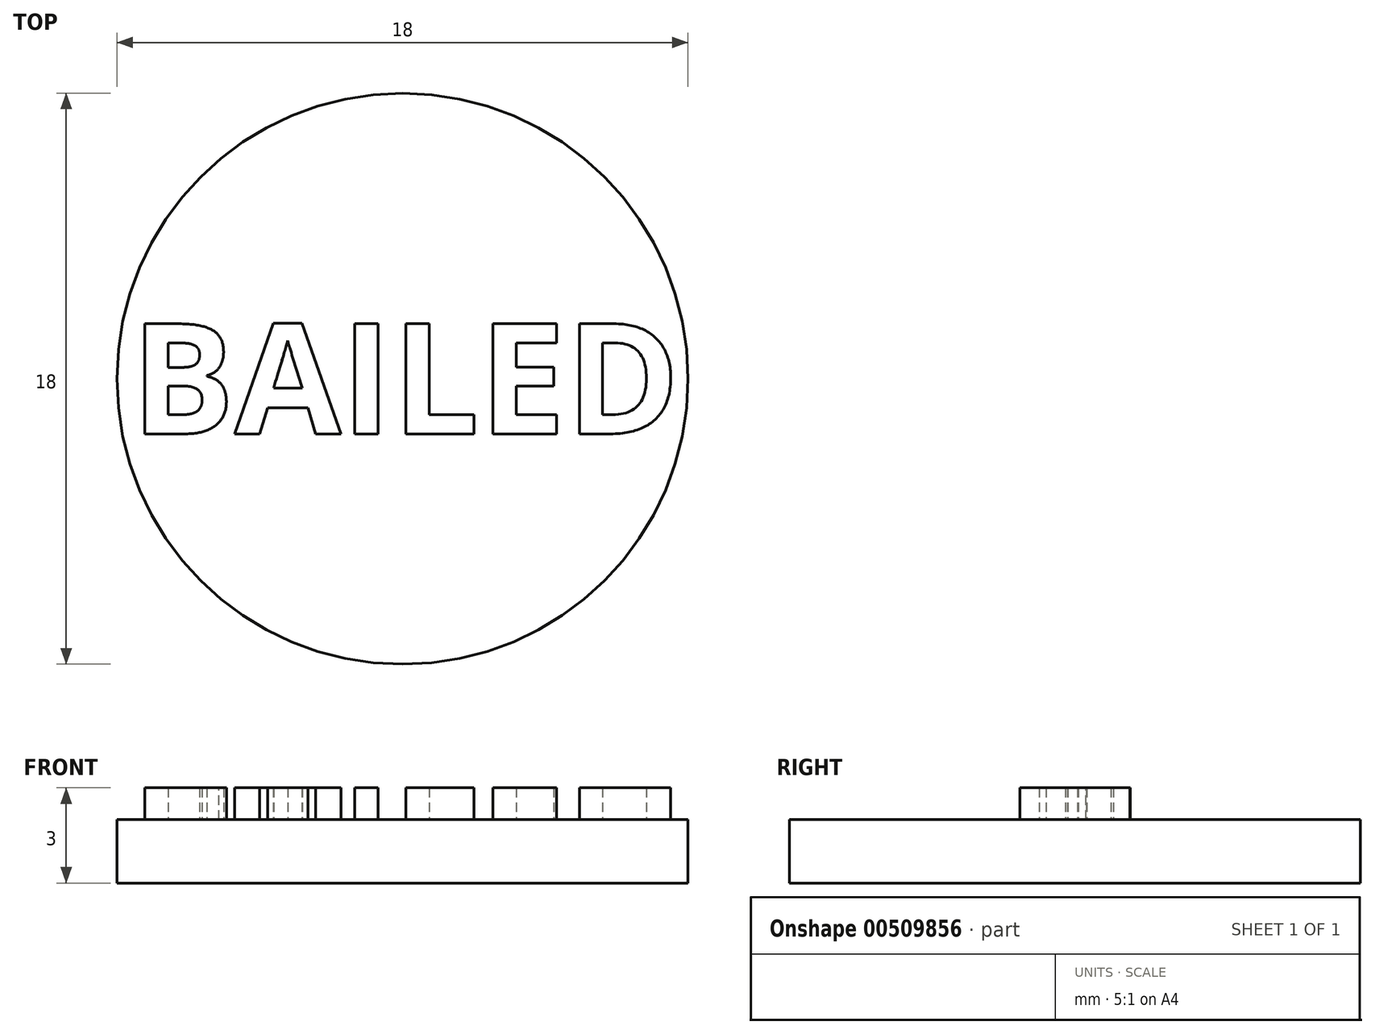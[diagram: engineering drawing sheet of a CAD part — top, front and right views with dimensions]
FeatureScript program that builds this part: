
annotation { "Feature Type Name" : "Feature", "Feature Type Description" : "" }
export const myFeature = defineFeature(function(context is Context, id is Id, definition is map)
    precondition{}
    {
        {
            var Q0;
            Q0=qCreatedBy(makeId("Top.planeOp"),FACE);
            var sketch = newSketch(context, id + "F0", { "sketchPlane" : qUnion([Q0])});
            skCircle(sketch, "E0", {"center": v(-38.86, 55.7) * mm, "radius": 9 * mm});
            skSolve(sketch);
        }
        {
            var Q0;
            Q0 = qSketchRegion(id + "F0", true);
            extrude(context, id + "F1", {"entities" : qUnion([Q0]), "depth" : 2 * mm, "offsetDistance" : 25 * mm});
        }
        {
            var Q0;
            Q0=makeQuery(id+"F1.opExtrude","CAP_FACE",FACE,{"disambiguationData":[OSD([sQuery(id+"F0.wireOp",EDGE,"E0")])],"isStart":false});
            var sketch = newSketch(context, id + "F2", { "sketchPlane" : qUnion([Q0])});
            skText(sketch, "E1", { "text": "BAILED", "fontName": "OpenSans-Bold.ttf"});
            const initialGuessF2  = {"E1": [-0.04742, 0.05396, 1, 0, 0.0035]};
            skSetInitialGuess(sketch, initialGuessF2);
            skSolve(sketch);
        }
        {
            var Q0;
            Q0 = qSketchRegion(id + "F2", true);
            extrude(context, id + "F3", {"entities" : qUnion([Q0]), "operationType" : NewBodyOperationType.ADD, "depth" : 1 * mm, "offsetDistance" : 25 * mm});
        }
    });
